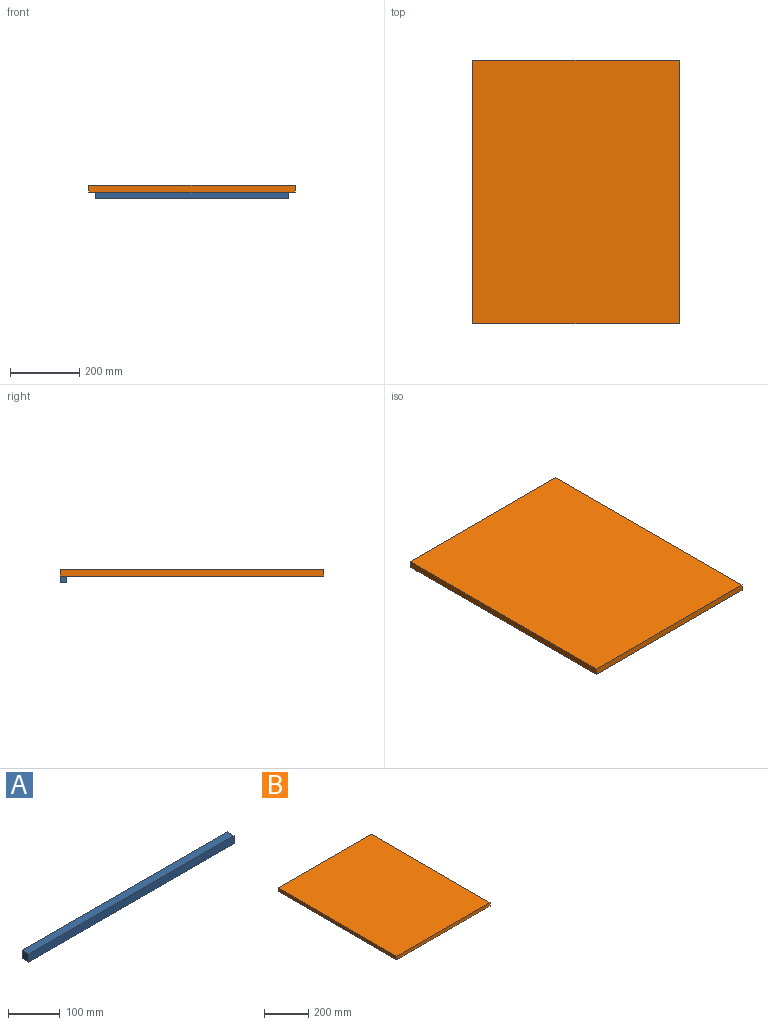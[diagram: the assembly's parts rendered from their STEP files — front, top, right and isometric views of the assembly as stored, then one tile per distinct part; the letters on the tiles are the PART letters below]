
ASSEMBLY  parts=2 mates=1
PART A: 6 faces, bbox 558.8x19.1x19.1 mm
  f0: plane 19.05x19.05mm, normal (-1,0,0), area 362.9mm2, adj f1,f3,f4,f5
  f1: plane 558.8x19.05mm, normal (0,-1,0), area 10645.1mm2, adj f0,f2,f4,f5
  f2: plane 19.05x19.05mm, normal (1,0,0), area 362.9mm2, adj f1,f3,f4,f5
  f3: plane 558.8x19.05mm, normal (0,1,0), area 10645.1mm2, adj f0,f2,f4,f5
  f4: plane 558.8x19.05mm, normal (0,0,1), area 10645.1mm2, adj f0,f1,f2,f3
  f5: plane 558.8x19.05mm, normal (0,0,-1), area 10645.1mm2, adj f0,f1,f2,f3
PART B: 6 faces, bbox 596.9x762x19.1 mm
  f0: plane 762x596.9mm, normal (0,0,1), area 454837.8mm2, adj f1,f3,f4,f5
  f1: plane 762x19.05mm, normal (-1,0,0), area 14516.1mm2, adj f0,f2,f4,f5
  f2: plane 762x596.9mm, normal (0,0,-1), area 454837.8mm2, adj f1,f3,f4,f5
  f3: plane 762x19.05mm, normal (1,0,0), area 14516.1mm2, adj f0,f2,f4,f5
  f4: plane 596.9x19.05mm, normal (0,-1,0), area 11370.9mm2, adj f0,f1,f2,f3
  f5: plane 596.9x19.05mm, normal (0,1,0), area 11370.9mm2, adj f0,f1,f2,f3
PLACE A t=(-74.51,373.79,-68.49)mm
PLACE B t=(-310.35,-71,-73.5)mm
MATE fastened A.f4 <-> B.f2  axis (0,0,1) through (-76.88,310,-49.44)mm
